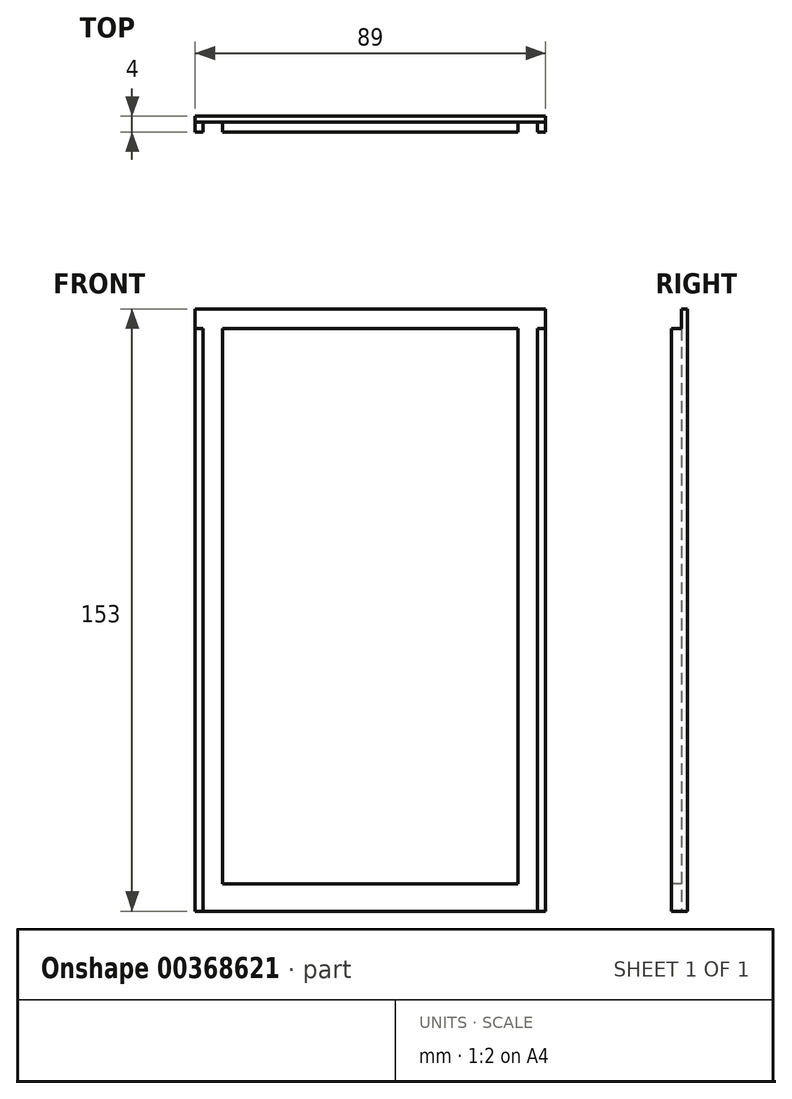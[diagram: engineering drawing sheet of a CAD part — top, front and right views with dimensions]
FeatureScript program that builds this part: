
annotation { "Feature Type Name" : "Feature", "Feature Type Description" : "" }
export const myFeature = defineFeature(function(context is Context, id is Id, definition is map)
    precondition{}
    {
        {
            var Q0;
            Q0=qCreatedBy(makeId("Front.planeOp"),FACE);
            var sketch = newSketch(context, id + "F0", { "sketchPlane" : qUnion([Q0])});
            skLineSegment(sketch, "E0.bottom", {"start": v(44.5, -76.5) * mm, "end": v(-44.5, -76.5) * mm});
            skLineSegment(sketch, "E0.top", {"start": v(44.5, 76.5) * mm, "end": v(-44.5, 76.5) * mm});
            skLineSegment(sketch, "E0.left", {"start": v(44.5, -76.5) * mm, "end": v(44.5, 76.5) * mm});
            skLineSegment(sketch, "E0.right", {"start": v(-44.5, -76.5) * mm, "end": v(-44.5, 76.5) * mm});
            skPoint(sketch, "E0.middle", {"position": v(0, 0) * mm});
            skSolve(sketch);
        }
        {
            var Q0;
            Q0=qSketchRegion(id+"F0",true);
            extrude(context, id + "F1", {"entities" : qUnion([Q0]), "depth" : 4 * mm});
        }
        {
            var Q0;
            Q0=makeQuery(id+"F1.opExtrude","CAP_FACE",FACE,{"disambiguationData":[OSD([sQuery(id+"F0.wireOp",EDGE,"E0.bottom"),sQuery(id+"F0.wireOp",EDGE,"E0.top"),sQuery(id+"F0.wireOp",EDGE,"E0.left"),sQuery(id+"F0.wireOp",EDGE,"E0.right")])],"isStart":false});
            var sketch = newSketch(context, id + "F2", { "sketchPlane" : qUnion([Q0])});
            skLineSegment(sketch, "E1.bottom", {"start": v(-42.5, 76.5) * mm, "end": v(-37.5, 76.5) * mm});
            skLineSegment(sketch, "E1.top", {"start": v(-42.5, -76.5) * mm, "end": v(-37.5, -76.5) * mm});
            skLineSegment(sketch, "E1.left", {"start": v(-42.5, 76.5) * mm, "end": v(-42.5, -76.5) * mm});
            skLineSegment(sketch, "E1.right", {"start": v(-37.5, 76.5) * mm, "end": v(-37.5, -76.5) * mm});
            skLineSegment(sketch, "E2.bottom", {"start": v(42.5, 76.5) * mm, "end": v(37.5, 76.5) * mm});
            skLineSegment(sketch, "E2.top", {"start": v(42.5, -76.5) * mm, "end": v(37.5, -76.5) * mm});
            skLineSegment(sketch, "E2.left", {"start": v(42.5, 76.5) * mm, "end": v(42.5, -76.5) * mm});
            skLineSegment(sketch, "E2.right", {"start": v(37.5, 76.5) * mm, "end": v(37.5, -76.5) * mm});
            skLineSegment(sketch, "E3.bottom", {"start": v(-37.5, -76.5) * mm, "end": v(37.5, -76.5) * mm});
            skLineSegment(sketch, "E3.top", {"start": v(-37.5, -69.5) * mm, "end": v(37.5, -69.5) * mm});
            skLineSegment(sketch, "E3.left", {"start": v(-37.5, -76.5) * mm, "end": v(-37.5, -69.5) * mm});
            skLineSegment(sketch, "E3.right", {"start": v(37.5, -76.5) * mm, "end": v(37.5, -69.5) * mm});
            skLineSegment(sketch, "E4.left", {"start": v(-37.5, 76.5) * mm, "end": v(-37.5, 71.5) * mm});
            skLineSegment(sketch, "E5.bottom", {"start": v(-44.5, 76.5) * mm, "end": v(44.5, 76.5) * mm});
            skLineSegment(sketch, "E5.top", {"start": v(-44.5, 71.5) * mm, "end": v(44.5, 71.5) * mm});
            skLineSegment(sketch, "E5.left", {"start": v(-44.5, 76.5) * mm, "end": v(-44.5, 71.5) * mm});
            skLineSegment(sketch, "E5.right", {"start": v(44.5, 76.5) * mm, "end": v(44.5, 71.5) * mm});
            skSolve(sketch);
        }
        {
            var Q0;
            Q0=qSketchRegion(id+"F2",true);
            extrude(context, id + "F3", {"entities" : qUnion([Q0]), "operationType" : NewBodyOperationType.REMOVE, "oppositeDirection" : true, "depth" : 2.5 * mm});
        }
    });
